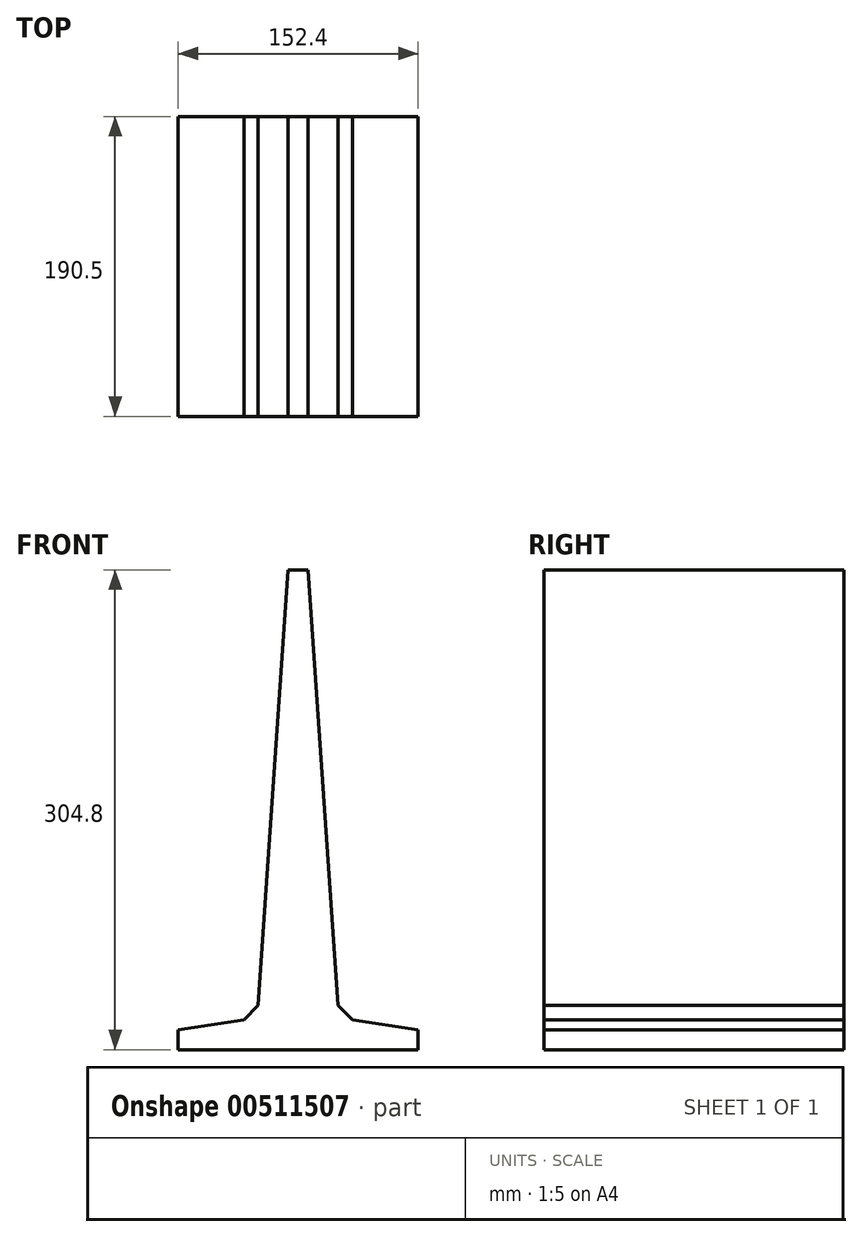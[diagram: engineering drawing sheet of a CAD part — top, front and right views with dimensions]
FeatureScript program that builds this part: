
annotation { "Feature Type Name" : "Feature", "Feature Type Description" : "" }
export const myFeature = defineFeature(function(context is Context, id is Id, definition is map)
    precondition{}
    {
        {
            var Q0;
            Q0=qCreatedBy(makeId("Front.planeOp"),FACE);
            var sketch = newSketch(context, id + "F0", { "sketchPlane" : qUnion([Q0])});
            skLineSegment(sketch, "E0", {"start": v(-76.2, 0) * mm, "end": v(76.2, 0) * mm});
            skLineSegment(sketch, "E1", {"start": v(76.2, 0) * mm, "end": v(76.2, 12.7) * mm});
            skLineSegment(sketch, "E2", {"start": v(76.2, 12.7) * mm, "end": v(34.38, 19.05) * mm});
            skLineSegment(sketch, "E3", {"start": v(34.38, 19.05) * mm, "end": v(25.4, 28.03) * mm});
            skLineSegment(sketch, "E4", {"start": v(25.4, 28.03) * mm, "end": v(6.35, 304.8) * mm});
            skLineSegment(sketch, "E5", {"start": v(6.35, 304.8) * mm, "end": v(-6.35, 304.8) * mm});
            skLineSegment(sketch, "E6", {"start": v(-6.35, 304.8) * mm, "end": v(-25.4, 28.03) * mm});
            skLineSegment(sketch, "E7", {"start": v(-25.4, 28.03) * mm, "end": v(-34.38, 19.05) * mm});
            skLineSegment(sketch, "E8", {"start": v(-34.38, 19.05) * mm, "end": v(-76.2, 12.7) * mm});
            skLineSegment(sketch, "E9", {"start": v(-76.2, 12.7) * mm, "end": v(-76.2, 0) * mm});
            skSolve(sketch);
        }
        {
            var Q0;
            Q0=makeQuery(id+"F0.imprint","IMPRINT",FACE,{"disambiguationData":[TD([[makeQuery(id+"F0.imprint","IMPRINT",EDGE,{"derivedFrom":sQuery(id+"F0.wireOp",EDGE,"E0")}),1.0]])]});
            extrude(context, id + "F1", {"entities" : qUnion([Q0]), "endBound" : BoundingType.SYMMETRIC, "depth" : 190.5 * mm});
        }
    });
